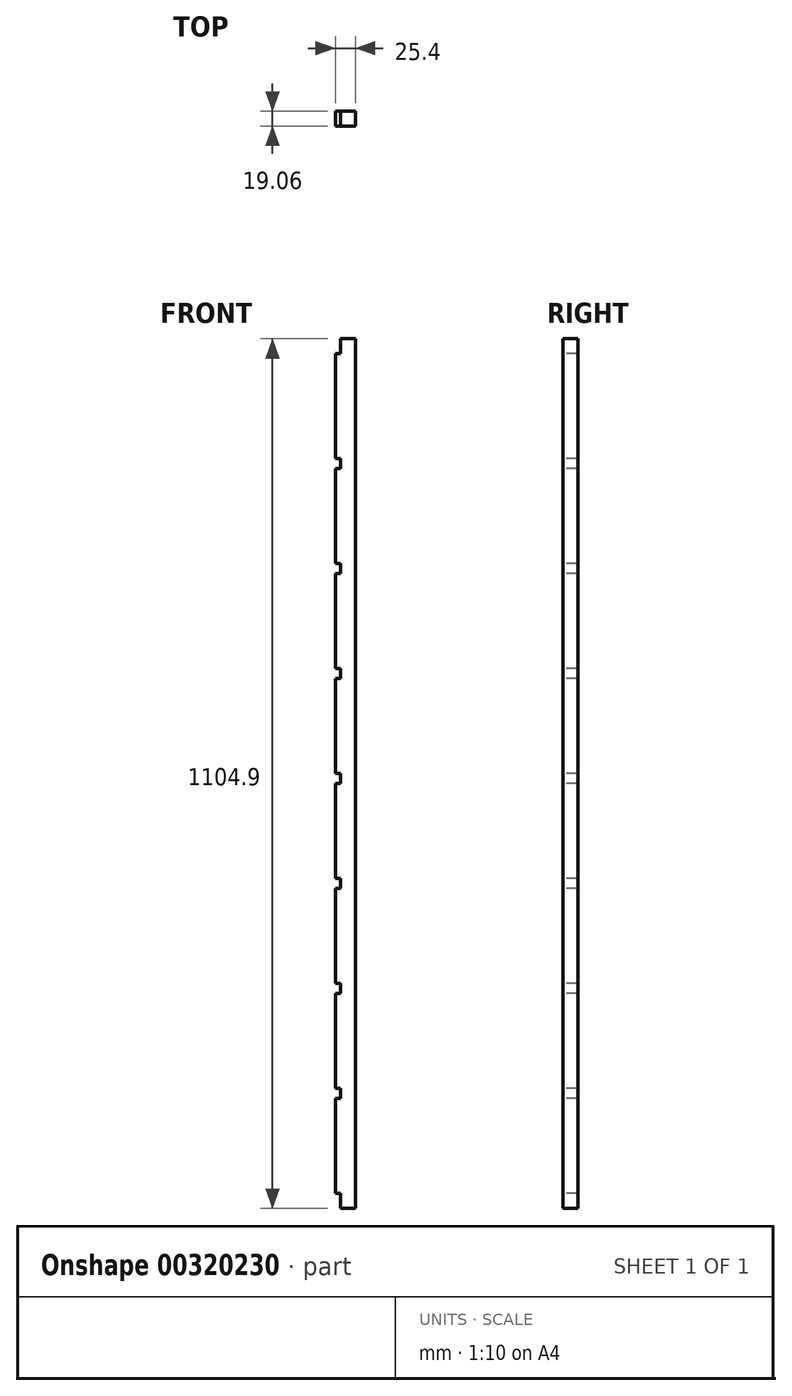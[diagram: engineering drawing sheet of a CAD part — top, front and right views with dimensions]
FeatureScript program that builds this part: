
annotation { "Feature Type Name" : "Feature", "Feature Type Description" : "" }
export const myFeature = defineFeature(function(context is Context, id is Id, definition is map)
    precondition{}
    {
        {
            var Q0;
            Q0=qCreatedBy(makeId("Top.planeOp"),FACE);
            var sketch = newSketch(context, id + "F0", { "sketchPlane" : qUnion([Q0])});
            skLineSegment(sketch, "E0.bottom", {"start": v(12.7, -9.53) * mm, "end": v(-12.7, -9.53) * mm});
            skLineSegment(sketch, "E0.top", {"start": v(12.7, 9.53) * mm, "end": v(-12.7, 9.52) * mm});
            skLineSegment(sketch, "E0.left", {"start": v(12.7, -9.53) * mm, "end": v(12.7, 9.53) * mm});
            skLineSegment(sketch, "E0.right", {"start": v(-12.7, -9.53) * mm, "end": v(-12.7, 9.52) * mm});
            skPoint(sketch, "E0.middle", {"position": v(0, 0) * mm});
            skSolve(sketch);
        }
        {
            var Q0;
            Q0 = qSketchRegion(id + "F0", true);
            extrude(context, id + "F1", {"entities" : qUnion([Q0]), "depth" : 1104.9 * mm});
        }
        {
            var Q0;
            Q0=makeQuery(id+"F1.opExtrude","SWEPT_FACE",FACE,{"disambiguationData":[OSD([sQuery(id+"F0.wireOp",EDGE,"E0.bottom")])]});
            var sketch = newSketch(context, id + "F2", { "sketchPlane" : qUnion([Q0])});
            skLineSegment(sketch, "E1.bottom", {"start": v(-12.7, 0) * mm, "end": v(-6.35, 0) * mm});
            skLineSegment(sketch, "E1.top", {"start": v(-12.7, 19.05) * mm, "end": v(-6.35, 19.05) * mm});
            skLineSegment(sketch, "E1.left", {"start": v(-12.7, 0) * mm, "end": v(-12.7, 19.05) * mm});
            skLineSegment(sketch, "E1.right", {"start": v(-6.35, 0) * mm, "end": v(-6.35, 19.05) * mm});
            skLineSegment(sketch, "E2.bottom", {"start": v(-12.7, 139.7) * mm, "end": v(-6.35, 139.7) * mm});
            skLineSegment(sketch, "E2.top", {"start": v(-12.7, 152.4) * mm, "end": v(-6.35, 152.4) * mm});
            skLineSegment(sketch, "E2.left", {"start": v(-12.7, 139.7) * mm, "end": v(-12.7, 152.4) * mm});
            skLineSegment(sketch, "E2.right", {"start": v(-6.35, 139.7) * mm, "end": v(-6.35, 152.4) * mm});
            skLineSegment(sketch, "E3.bottom", {"start": v(-12.7, 273.05) * mm, "end": v(-6.35, 273.05) * mm});
            skLineSegment(sketch, "E3.top", {"start": v(-12.7, 285.75) * mm, "end": v(-6.35, 285.75) * mm});
            skLineSegment(sketch, "E3.left", {"start": v(-12.7, 273.05) * mm, "end": v(-12.7, 285.75) * mm});
            skLineSegment(sketch, "E3.right", {"start": v(-6.35, 273.05) * mm, "end": v(-6.35, 285.75) * mm});
            skLineSegment(sketch, "E4.bottom", {"start": v(-12.7, 406.4) * mm, "end": v(-6.35, 406.4) * mm});
            skLineSegment(sketch, "E4.top", {"start": v(-12.7, 419.1) * mm, "end": v(-6.35, 419.1) * mm});
            skLineSegment(sketch, "E4.left", {"start": v(-12.7, 406.4) * mm, "end": v(-12.7, 419.1) * mm});
            skLineSegment(sketch, "E4.right", {"start": v(-6.35, 406.4) * mm, "end": v(-6.35, 419.1) * mm});
            skLineSegment(sketch, "E5.bottom", {"start": v(-12.7, 539.75) * mm, "end": v(-6.35, 539.75) * mm});
            skLineSegment(sketch, "E5.top", {"start": v(-12.7, 552.45) * mm, "end": v(-6.35, 552.45) * mm});
            skLineSegment(sketch, "E5.left", {"start": v(-12.7, 539.75) * mm, "end": v(-12.7, 552.45) * mm});
            skLineSegment(sketch, "E5.right", {"start": v(-6.35, 539.75) * mm, "end": v(-6.35, 552.45) * mm});
            skLineSegment(sketch, "E6.bottom", {"start": v(-12.7, 673.1) * mm, "end": v(-6.35, 673.1) * mm});
            skLineSegment(sketch, "E6.top", {"start": v(-12.7, 685.8) * mm, "end": v(-6.35, 685.8) * mm});
            skLineSegment(sketch, "E6.left", {"start": v(-12.7, 673.1) * mm, "end": v(-12.7, 685.8) * mm});
            skLineSegment(sketch, "E6.right", {"start": v(-6.35, 673.1) * mm, "end": v(-6.35, 685.8) * mm});
            skLineSegment(sketch, "E7.bottom", {"start": v(-12.7, 806.45) * mm, "end": v(-6.35, 806.45) * mm});
            skLineSegment(sketch, "E7.top", {"start": v(-12.7, 819.15) * mm, "end": v(-6.35, 819.15) * mm});
            skLineSegment(sketch, "E7.left", {"start": v(-12.7, 806.45) * mm, "end": v(-12.7, 819.15) * mm});
            skLineSegment(sketch, "E7.right", {"start": v(-6.35, 806.45) * mm, "end": v(-6.35, 819.15) * mm});
            skLineSegment(sketch, "E8.bottom", {"start": v(-12.7, 939.8) * mm, "end": v(-6.35, 939.8) * mm});
            skLineSegment(sketch, "E8.top", {"start": v(-12.7, 952.5) * mm, "end": v(-6.35, 952.5) * mm});
            skLineSegment(sketch, "E8.left", {"start": v(-12.7, 939.8) * mm, "end": v(-12.7, 952.5) * mm});
            skLineSegment(sketch, "E8.right", {"start": v(-6.35, 939.8) * mm, "end": v(-6.35, 952.5) * mm});
            skLineSegment(sketch, "E9.bottom", {"start": v(-12.7, 1104.9) * mm, "end": v(-6.35, 1104.9) * mm});
            skLineSegment(sketch, "E9.top", {"start": v(-12.7, 1085.85) * mm, "end": v(-6.35, 1085.85) * mm});
            skLineSegment(sketch, "E9.left", {"start": v(-12.7, 1104.9) * mm, "end": v(-12.7, 1085.85) * mm});
            skLineSegment(sketch, "E9.right", {"start": v(-6.35, 1104.9) * mm, "end": v(-6.35, 1085.85) * mm});
            skSolve(sketch);
        }
        {
            var Q0;
            Q0=makeQuery(id+"F2.imprint","IMPRINT",FACE,{"disambiguationData":[TD([[makeQuery(id+"F2.imprint","IMPRINT",EDGE,{"derivedFrom":sQuery(id+"F2.wireOp",EDGE,"E1.bottom")}),-1.0]])]});
            var Q1;
            Q1=makeQuery(id+"F2.imprint","IMPRINT",FACE,{"disambiguationData":[TD([[makeQuery(id+"F2.imprint","IMPRINT",EDGE,{"derivedFrom":sQuery(id+"F2.wireOp",EDGE,"E2.bottom")}),1.0]])]});
            var Q2;
            Q2=makeQuery(id+"F2.imprint","IMPRINT",FACE,{"disambiguationData":[TD([[makeQuery(id+"F2.imprint","IMPRINT",EDGE,{"derivedFrom":sQuery(id+"F2.wireOp",EDGE,"E3.bottom")}),1.0]])]});
            var Q3;
            Q3=makeQuery(id+"F2.imprint","IMPRINT",FACE,{"disambiguationData":[TD([[makeQuery(id+"F2.imprint","IMPRINT",EDGE,{"derivedFrom":sQuery(id+"F2.wireOp",EDGE,"E4.bottom")}),1.0]])]});
            var Q4;
            Q4=makeQuery(id+"F2.imprint","IMPRINT",FACE,{"disambiguationData":[TD([[makeQuery(id+"F2.imprint","IMPRINT",EDGE,{"derivedFrom":sQuery(id+"F2.wireOp",EDGE,"E5.bottom")}),1.0]])]});
            var Q5;
            Q5=makeQuery(id+"F2.imprint","IMPRINT",FACE,{"disambiguationData":[TD([[makeQuery(id+"F2.imprint","IMPRINT",EDGE,{"derivedFrom":sQuery(id+"F2.wireOp",EDGE,"E6.bottom")}),1.0]])]});
            var Q6;
            Q6=makeQuery(id+"F2.imprint","IMPRINT",FACE,{"disambiguationData":[TD([[makeQuery(id+"F2.imprint","IMPRINT",EDGE,{"derivedFrom":sQuery(id+"F2.wireOp",EDGE,"E7.bottom")}),1.0]])]});
            var Q7;
            Q7=makeQuery(id+"F2.imprint","IMPRINT",FACE,{"disambiguationData":[TD([[makeQuery(id+"F2.imprint","IMPRINT",EDGE,{"derivedFrom":sQuery(id+"F2.wireOp",EDGE,"E8.bottom")}),1.0]])]});
            var Q8;
            {var subQ0=sQuery(id+"F2.wireOp",EDGE,"E9.bottom");Q8=makeQuery(id+"F2.imprint","IMPRINT",FACE,{"disambiguationData":[TD([[makeQuery(id+"F2.imprint","IMPRINT",EDGE,{"derivedFrom":subQ0}),1.0]])]});}
            extrude(context, id + "F3", {"entities" : qUnion([Q0, Q1, Q2, Q3, Q4, Q5, Q6, Q7, Q8]), "operationType" : NewBodyOperationType.REMOVE, "endBound" : BoundingType.THROUGH_ALL, "oppositeDirection" : true, "depth" : 25.4 * mm});
        }
    });
